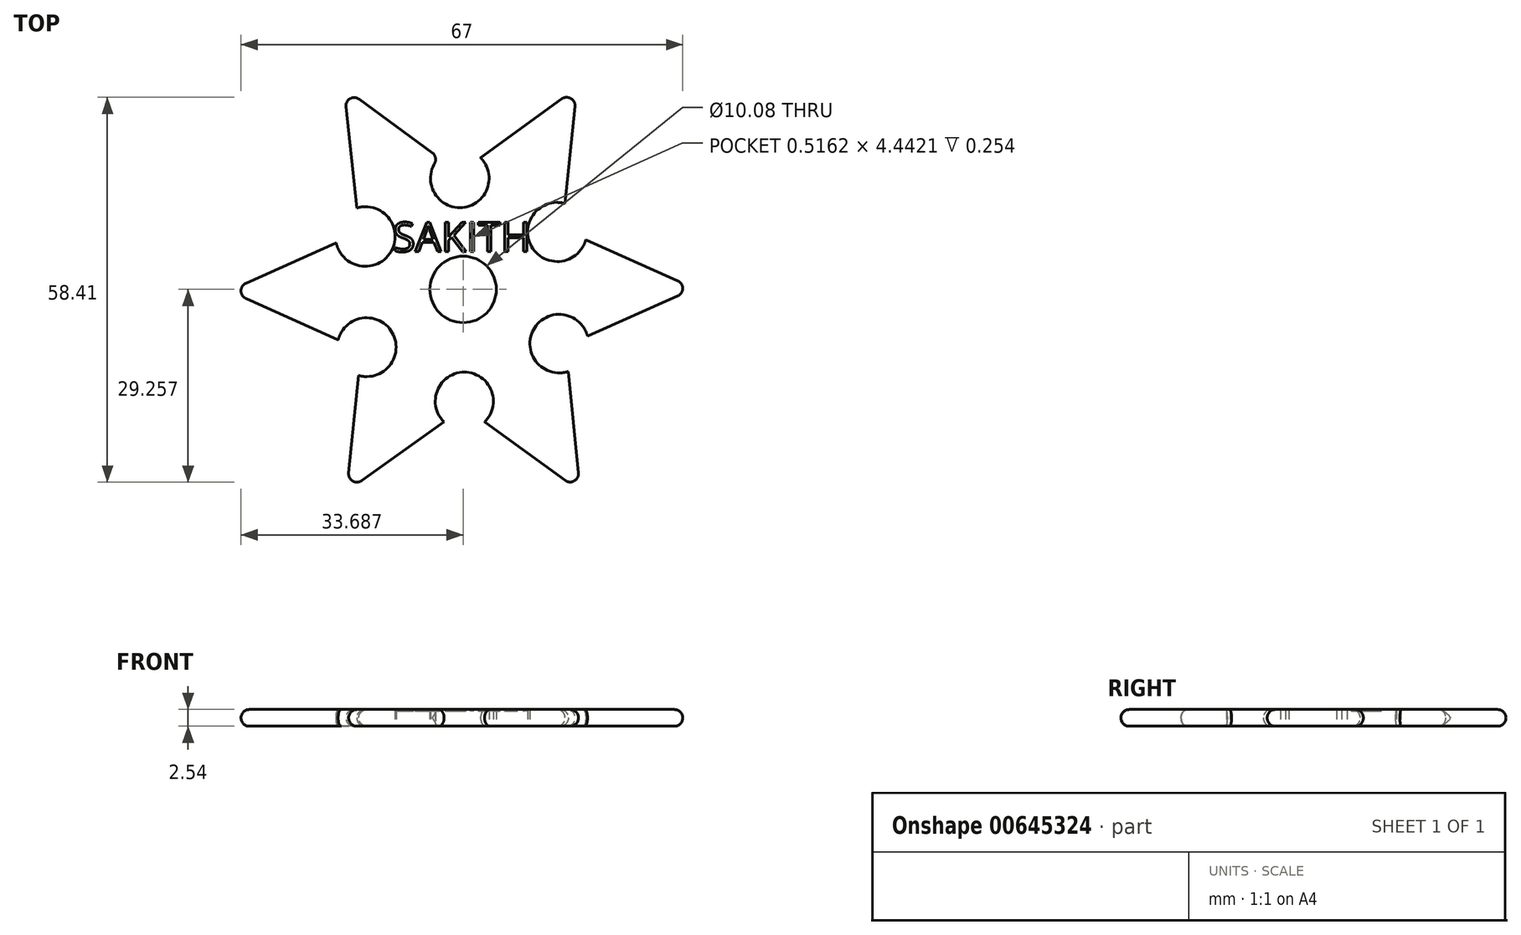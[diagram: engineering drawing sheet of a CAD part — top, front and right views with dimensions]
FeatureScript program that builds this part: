
annotation { "Feature Type Name" : "Feature", "Feature Type Description" : "" }
export const myFeature = defineFeature(function(context is Context, id is Id, definition is map)
    precondition{}
    {
        {
            var Q0;
            Q0=qCreatedBy(makeId("Top.planeOp"),FACE);
            var sketch = newSketch(context, id + "F0", { "sketchPlane" : qUnion([Q0])});
            skLineSegment(sketch, "E0", {"start": v(20.76, 43.43) * mm, "end": v(18.8, 61.65) * mm});
            skLineSegment(sketch, "E1", {"start": v(18.8, 61.65) * mm, "end": v(33.23, 51.05) * mm});
            skLineSegment(sketch, "E2", {"start": v(39.52, 51.05) * mm, "end": v(54.14, 61.65) * mm});
            skLineSegment(sketch, "E3", {"start": v(54.14, 61.65) * mm, "end": v(52.35, 44.11) * mm});
            skLineSegment(sketch, "E4", {"start": v(55.48, 38.6) * mm, "end": v(72.05, 31.23) * mm});
            skLineSegment(sketch, "E5", {"start": v(72.05, 31.23) * mm, "end": v(55.74, 24) * mm});
            skLineSegment(sketch, "E6", {"start": v(52.84, 18.62) * mm, "end": v(54.65, 0.42) * mm});
            skLineSegment(sketch, "E7", {"start": v(54.65, 0.42) * mm, "end": v(40.12, 10.94) * mm});
            skLineSegment(sketch, "E8", {"start": v(34, 10.94) * mm, "end": v(19.23, 0.42) * mm});
            skLineSegment(sketch, "E9", {"start": v(19.23, 0.42) * mm, "end": v(21.04, 18) * mm});
            skLineSegment(sketch, "E10", {"start": v(17.93, 23.43) * mm, "end": v(1.35, 30.85) * mm});
            skLineSegment(sketch, "E11", {"start": v(1.35, 30.85) * mm, "end": v(17.63, 38.13) * mm});
            skArc(sketch, "E12", {"start": v(17.63, 38.13) * mm, "mid": v(25.94, 36.8) * mm, "end": v(20.76, 43.43) * mm});
            skArc(sketch, "E13", {"start": v(33.23, 51.05) * mm, "mid": v(36.37, 43.47) * mm, "end": v(39.52, 51.05) * mm});
            skArc(sketch, "E14", {"start": v(52.35, 44.11) * mm, "mid": v(47.26, 37.57) * mm, "end": v(55.48, 38.6) * mm});
            skArc(sketch, "E15", {"start": v(55.74, 24) * mm, "mid": v(47.54, 24.95) * mm, "end": v(52.84, 18.62) * mm});
            skArc(sketch, "E16", {"start": v(40.12, 10.94) * mm, "mid": v(37.06, 18.5) * mm, "end": v(34, 10.94) * mm});
            skArc(sketch, "E17", {"start": v(21.04, 18) * mm, "mid": v(26.12, 24.51) * mm, "end": v(17.93, 23.43) * mm});
            skCircle(sketch, "E18", {"center": v(36.88, 31.07) * mm, "radius": 5.04 * mm});
            skPoint(sketch, "E18.first.point", {"position": v(36.65, 36.1) * mm});
            skPoint(sketch, "E18.second.point", {"position": v(36.92, 26.03) * mm});
            skPoint(sketch, "E18.third.point", {"position": v(36.84, 26.03) * mm});
            skSolve(sketch);
        }
        {
            var Q0;
            Q0 = qSketchRegion(id + "F0", true);
            extrude(context, id + "F1", {"entities" : qUnion([Q0]), "depth" : 2.54 * mm, "offsetDistance" : 25.4 * mm});
        }
        {
            var Q0;
            Q0=makeQuery(id+"F1.opExtrude","CAP_FACE",FACE,{"disambiguationData":[OSD([sQuery(id+"F0.wireOp",EDGE,"E0"),sQuery(id+"F0.wireOp",EDGE,"E1"),sQuery(id+"F0.wireOp",EDGE,"E2"),sQuery(id+"F0.wireOp",EDGE,"E3"),sQuery(id+"F0.wireOp",EDGE,"E4"),sQuery(id+"F0.wireOp",EDGE,"E5"),sQuery(id+"F0.wireOp",EDGE,"E6"),sQuery(id+"F0.wireOp",EDGE,"E7"),sQuery(id+"F0.wireOp",EDGE,"E8"),sQuery(id+"F0.wireOp",EDGE,"E9"),sQuery(id+"F0.wireOp",EDGE,"E10"),sQuery(id+"F0.wireOp",EDGE,"E11"),sQuery(id+"F0.wireOp",EDGE,"E12"),sQuery(id+"F0.wireOp",EDGE,"E13"),sQuery(id+"F0.wireOp",EDGE,"E14"),sQuery(id+"F0.wireOp",EDGE,"E15"),sQuery(id+"F0.wireOp",EDGE,"E16"),sQuery(id+"F0.wireOp",EDGE,"E17"),sQuery(id+"F0.wireOp",EDGE,"E18")])],"isStart":false});
            var sketch = newSketch(context, id + "F2", { "sketchPlane" : qUnion([Q0])});
            skText(sketch, "E19", { "text": "SAKITH", "fontName": "OpenSans-Regular.ttf"});
            const initialGuessF2  = {"E19": [0.0262, 0.0368, 1, 0, 0.00448]};
            skSetInitialGuess(sketch, initialGuessF2);
            skSolve(sketch);
        }
        {
            var Q0;
            Q0 = qSketchRegion(id + "F2", true);
            extrude(context, id + "F3", {"entities" : qUnion([Q0]), "operationType" : NewBodyOperationType.REMOVE, "oppositeDirection" : true, "depth" : 0.25 * mm, "offsetDistance" : 25.4 * mm});
        }
        {
            var Q0;
            Q0=makeQuery(id+"F1.opExtrude","CAP_EDGE",EDGE,{"disambiguationData":[OSD([sQuery(id+"F0.wireOp",EDGE,"E1")])],"isStart":false});
            var Q1;
            Q1=makeQuery(id+"F1.opExtrude","CAP_EDGE",EDGE,{"disambiguationData":[OSD([sQuery(id+"F0.wireOp",EDGE,"E1")])],"isStart":true});
            var Q2;
            Q2=makeQuery(id+"F1.opExtrude","CAP_EDGE",EDGE,{"disambiguationData":[OSD([sQuery(id+"F0.wireOp",EDGE,"E0")])],"isStart":false});
            var Q3;
            Q3=makeQuery(id+"F1.opExtrude","CAP_EDGE",EDGE,{"disambiguationData":[OSD([sQuery(id+"F0.wireOp",EDGE,"E0")])],"isStart":true});
            var Q4;
            Q4=makeQuery(id+"F1.opExtrude","SWEPT_FACE",FACE,{"disambiguationData":[OSD([sQuery(id+"F0.wireOp",EDGE,"E1")])]});
            var Q5;
            Q5=makeQuery(id+"F1.opExtrude","CAP_EDGE",EDGE,{"disambiguationData":[OSD([sQuery(id+"F0.wireOp",EDGE,"E10")])],"isStart":true});
            var Q6;
            Q6=makeQuery(id+"F1.opExtrude","CAP_EDGE",EDGE,{"disambiguationData":[OSD([sQuery(id+"F0.wireOp",EDGE,"E10")])],"isStart":false});
            var Q7;
            Q7=makeQuery(id+"F1.opExtrude","SWEPT_EDGE",EDGE,{"disambiguationData":[OSD([sQuery(id+"F0.wireOp",EDGE,"E10"),sQuery(id+"F0.wireOp",EDGE,"E11")])]});
            var Q8;
            Q8=makeQuery(id+"F1.opExtrude","CAP_EDGE",EDGE,{"disambiguationData":[OSD([sQuery(id+"F0.wireOp",EDGE,"E11")])],"isStart":false});
            var Q9;
            Q9=makeQuery(id+"F1.opExtrude","CAP_EDGE",EDGE,{"disambiguationData":[OSD([sQuery(id+"F0.wireOp",EDGE,"E11")])],"isStart":true});
            var Q10;
            Q10=makeQuery(id+"F1.opExtrude","SWEPT_EDGE",EDGE,{"disambiguationData":[OSD([sQuery(id+"F0.wireOp",EDGE,"E8"),sQuery(id+"F0.wireOp",EDGE,"E9")])]});
            var Q11;
            Q11=makeQuery(id+"F1.opExtrude","CAP_EDGE",EDGE,{"disambiguationData":[OSD([sQuery(id+"F0.wireOp",EDGE,"E9")])],"isStart":true});
            var Q12;
            Q12=makeQuery(id+"F1.opExtrude","CAP_EDGE",EDGE,{"disambiguationData":[OSD([sQuery(id+"F0.wireOp",EDGE,"E9")])],"isStart":false});
            var Q13;
            Q13=makeQuery(id+"F1.opExtrude","CAP_EDGE",EDGE,{"disambiguationData":[OSD([sQuery(id+"F0.wireOp",EDGE,"E8")])],"isStart":true});
            var Q14;
            Q14=makeQuery(id+"F1.opExtrude","CAP_EDGE",EDGE,{"disambiguationData":[OSD([sQuery(id+"F0.wireOp",EDGE,"E8")])],"isStart":false});
            var Q15;
            Q15=makeQuery(id+"F1.opExtrude","CAP_EDGE",EDGE,{"disambiguationData":[OSD([sQuery(id+"F0.wireOp",EDGE,"E7")])],"isStart":true});
            var Q16;
            Q16=makeQuery(id+"F1.opExtrude","SWEPT_EDGE",EDGE,{"disambiguationData":[OSD([sQuery(id+"F0.wireOp",EDGE,"E6"),sQuery(id+"F0.wireOp",EDGE,"E7")])]});
            var Q17;
            Q17=makeQuery(id+"F1.opExtrude","CAP_EDGE",EDGE,{"disambiguationData":[OSD([sQuery(id+"F0.wireOp",EDGE,"E7")])],"isStart":false});
            var Q18;
            Q18=makeQuery(id+"F1.opExtrude","CAP_EDGE",EDGE,{"disambiguationData":[OSD([sQuery(id+"F0.wireOp",EDGE,"E6")])],"isStart":true});
            var Q19;
            Q19=makeQuery(id+"F1.opExtrude","CAP_EDGE",EDGE,{"disambiguationData":[OSD([sQuery(id+"F0.wireOp",EDGE,"E6")])],"isStart":false});
            var Q20;
            Q20=makeQuery(id+"F1.opExtrude","CAP_EDGE",EDGE,{"disambiguationData":[OSD([sQuery(id+"F0.wireOp",EDGE,"E5")])],"isStart":false});
            var Q21;
            Q21=makeQuery(id+"F1.opExtrude","CAP_EDGE",EDGE,{"disambiguationData":[OSD([sQuery(id+"F0.wireOp",EDGE,"E5")])],"isStart":true});
            var Q22;
            Q22=makeQuery(id+"F1.opExtrude","SWEPT_EDGE",EDGE,{"disambiguationData":[OSD([sQuery(id+"F0.wireOp",EDGE,"E4"),sQuery(id+"F0.wireOp",EDGE,"E5")])]});
            var Q23;
            Q23=makeQuery(id+"F1.opExtrude","CAP_EDGE",EDGE,{"disambiguationData":[OSD([sQuery(id+"F0.wireOp",EDGE,"E4")])],"isStart":false});
            var Q24;
            Q24=makeQuery(id+"F1.opExtrude","CAP_EDGE",EDGE,{"disambiguationData":[OSD([sQuery(id+"F0.wireOp",EDGE,"E4")])],"isStart":true});
            var Q25;
            Q25=makeQuery(id+"F1.opExtrude","CAP_EDGE",EDGE,{"disambiguationData":[OSD([sQuery(id+"F0.wireOp",EDGE,"E2")])],"isStart":true});
            var Q26;
            Q26=makeQuery(id+"F1.opExtrude","CAP_EDGE",EDGE,{"disambiguationData":[OSD([sQuery(id+"F0.wireOp",EDGE,"E3")])],"isStart":false});
            var Q27;
            Q27=makeQuery(id+"F1.opExtrude","SWEPT_EDGE",EDGE,{"disambiguationData":[OSD([sQuery(id+"F0.wireOp",EDGE,"E2"),sQuery(id+"F0.wireOp",EDGE,"E3")])]});
            var Q28;
            Q28=makeQuery(id+"F1.opExtrude","CAP_EDGE",EDGE,{"disambiguationData":[OSD([sQuery(id+"F0.wireOp",EDGE,"E3")])],"isStart":true});
            var Q29;
            Q29=makeQuery(id+"F1.opExtrude","CAP_EDGE",EDGE,{"disambiguationData":[OSD([sQuery(id+"F0.wireOp",EDGE,"E2")])],"isStart":false});
            fillet(context, id + "F4", {"entities" : qUnion([Q0, Q1, Q2, Q3, Q4, Q5, Q6, Q7, Q8, Q9, Q10, Q11, Q12, Q13, Q14, Q15, Q16, Q17, Q18, Q19, Q20, Q21, Q22, Q23, Q24, Q25, Q26, Q27, Q28, Q29]), "radius" : 1.27 * mm, "tangentPropagation" : true, "allowEdgeOverflow" : false});
        }
    });
